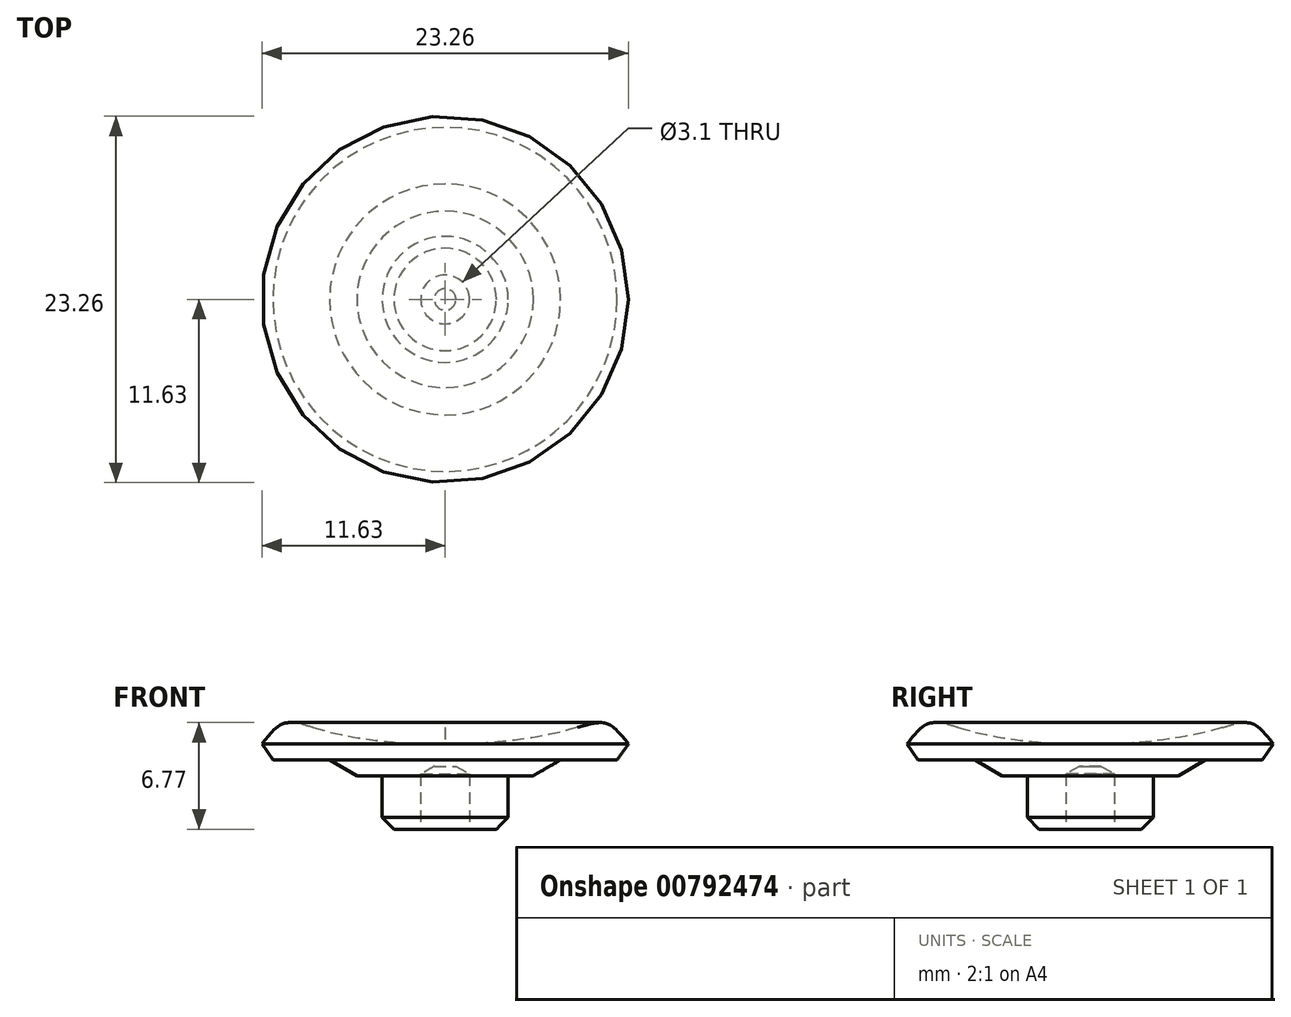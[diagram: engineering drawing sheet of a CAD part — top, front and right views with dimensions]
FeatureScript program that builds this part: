
annotation { "Feature Type Name" : "Feature", "Feature Type Description" : "" }
export const myFeature = defineFeature(function(context is Context, id is Id, definition is map)
    precondition{}
    {
        {
            var Q0;
            Q0=qCreatedBy(makeId("Right.planeOp"),FACE);
            var sketch = newSketch(context, id + "F0", { "sketchPlane" : qUnion([Q0])});
            skLineSegment(sketch, "E0", {"start": v(0, 0) * mm, "end": v(4, 0) * mm});
            skLineSegment(sketch, "E1", {"start": v(4, 0) * mm, "end": v(4, 4.4) * mm});
            skLineSegment(sketch, "E2", {"start": v(4, 4.4) * mm, "end": v(12, 4.4) * mm});
            skLineSegment(sketch, "E3", {"start": v(12, 4.4) * mm, "end": v(10.9, 7.4) * mm});
            skFitSpline(sketch, "E4", {"points": [v(10.9, 7.4) * mm, v(0, 5.4) * mm], "startDerivative": vector(-6.65, -3) * mm, "endDerivative": vector(-16.55, 0) * mm});
            skLineSegment(sketch, "E5", {"start": v(0, 5.4) * mm, "end": v(0, 0) * mm});
            skLineSegment(sketch, "E6", {"start": v(8.7, 6.4) * mm, "end": v(10.9, 7.4) * mm, "construction": true});
            skLineSegment(sketch, "E7", {"start": v(0, 5.4) * mm, "end": v(5.52, 5.4) * mm, "construction": true});
            skLineSegment(sketch, "E8", {"start": v(4, 3.4) * mm, "end": v(5.6, 3.4) * mm});
            skLineSegment(sketch, "E9", {"start": v(5.6, 3.4) * mm, "end": v(7.33, 4.4) * mm});
            skSolve(sketch);
        }
        {
            var Q0;
            Q0=makeQuery(id+"F0.imprint","IMPRINT",FACE,{"disambiguationData":[TD([[makeQuery(id+"F0.imprint","IMPRINT",EDGE,{"derivedFrom":sQuery(id+"F0.wireOp",EDGE,"E0")}),1.0]])]});
            var Q1;
            {var subQ3=sQuery(id+"F0.wireOp",EDGE,"E8");Q1=makeQuery(id+"F0.imprint","IMPRINT",FACE,{"disambiguationData":[TD([[makeQuery(id+"F0.imprint","IMPRINT",EDGE,{"derivedFrom":subQ3}),1.0]])]});}
            var Q2;
            Q2=sQuery(id+"F0.wireOp",EDGE,"E5");
            revolve(context, id + "F1", {"surfaceOperationType" : NewSurfaceOperationType.NEW, "entities" : qUnion([Q0, Q1]), "axis" : qUnion([Q2]), "revolveType" : RevolveType.FULL});
        }
        {
            var Q0;
            Q0=makeQuery(id+"F1.opRevolve","SWEPT_EDGE",EDGE,{"disambiguationData":[OSD([sQuery(id+"F0.wireOp",EDGE,"E2"),sQuery(id+"F0.wireOp",EDGE,"E3")])]});
            var Q1;
            Q1=makeQuery(id+"F1.opRevolve","SWEPT_EDGE",EDGE,{"disambiguationData":[OSD([sQuery(id+"F0.wireOp",EDGE,"E0"),sQuery(id+"F0.wireOp",EDGE,"E1")])]});
            chamfer(context, id + "F2", {"entities" : qUnion([Q0, Q1]), "width" : .75 * mm, "tangentPropagation" : true});
        }
        {
            var Q0;
            Q0=makeQuery(id+"F1.opRevolve","SWEPT_EDGE",EDGE,{"disambiguationData":[OSD([sQuery(id+"F0.wireOp",EDGE,"E3"),sQuery(id+"F0.wireOp",EDGE,"E4")])]});
            fillet(context, id + "F3", {"entities" : qUnion([Q0]), "radius" : 3 * mm, "tangentPropagation" : true, "rho" : .7, "crossSection" : FilletCrossSection.CONIC, "allowEdgeOverflow" : false});
        }
        {
            var Q0;
            Q0=makeQuery(id+"F1.opRevolve","SWEPT_FACE",FACE,{"disambiguationData":[OSD([sQuery(id+"F0.wireOp",EDGE,"E0")])]});
            var sketch = newSketch(context, id + "F4", { "sketchPlane" : qUnion([Q0])});
            skCircle(sketch, "E10", {"center": v(0, 0) * mm, "radius": 1.55 * mm});
            skSolve(sketch);
        }
        {
            var Q0;
            Q0=makeQuery(id+"F4.imprint","IMPRINT",FACE,{"disambiguationData":[TD([[makeQuery(id+"F4.imprint","IMPRINT",EDGE,{"derivedFrom":sQuery(id+"F4.wireOp",EDGE,"E10")}),1.0]])]});
            extrude(context, id + "F5", {"entities" : qUnion([Q0]), "operationType" : NewBodyOperationType.REMOVE, "oppositeDirection" : true, "depth" : 4 * mm, "offsetDistance" : 25 * mm});
        }
        {
            var Q0;
            Q0=makeQuery(id+"F5.boolean.opBoolean","COPY",EDGE,{"derivedFrom":makeQuery(id+"F5.opExtrude","CAP_EDGE",EDGE,{"disambiguationData":[OSD([sQuery(id+"F4.wireOp",EDGE,"E10")])],"isStart":false})});
            chamfer(context, id + "F6", {"entities" : qUnion([Q0]), "chamferType" : ChamferType.OFFSET_ANGLE, "width" : .5 * mm, "oppositeDirection" : true, "angle" : 60 * degree, "tangentPropagation" : true});
        }
    });
